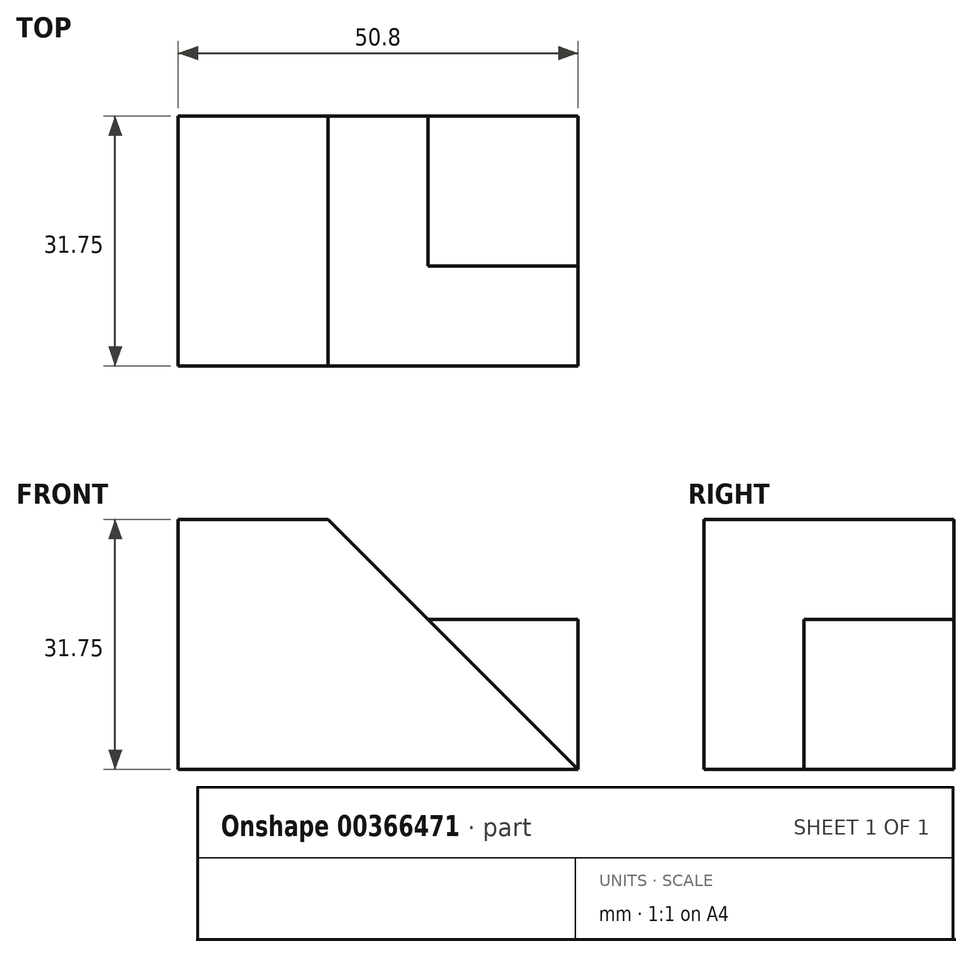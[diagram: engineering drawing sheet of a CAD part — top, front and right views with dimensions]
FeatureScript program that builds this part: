
annotation { "Feature Type Name" : "Feature", "Feature Type Description" : "" }
export const myFeature = defineFeature(function(context is Context, id is Id, definition is map)
    precondition{}
    {
        {
            var Q0;
            Q0=qCreatedBy(makeId("Front.planeOp"),FACE);
            var sketch = newSketch(context, id + "F0", { "sketchPlane" : qUnion([Q0])});
            skLineSegment(sketch, "E0", {"start": v(0, 0) * mm, "end": v(0, 31.75) * mm});
            skLineSegment(sketch, "E1", {"start": v(0, 31.75) * mm, "end": v(19.05, 31.75) * mm});
            skLineSegment(sketch, "E2", {"start": v(19.05, 31.75) * mm, "end": v(50.8, 0) * mm});
            skLineSegment(sketch, "E3", {"start": v(50.8, 0) * mm, "end": v(0, 0) * mm});
            skSolve(sketch);
        }
        {
            var Q0;
            Q0=makeQuery(id+"F0.imprint","IMPRINT",FACE,{"disambiguationData":[TD([[makeQuery(id+"F0.imprint","IMPRINT",EDGE,{"derivedFrom":sQuery(id+"F0.wireOp",EDGE,"E0")}),-1.0]])]});
            extrude(context, id + "F1", {"entities" : qUnion([Q0]), "oppositeDirection" : true, "depth" : 31.75 * mm});
        }
        {
            var Q0;
            Q0=makeQuery(id+"F1.opExtrude","CAP_FACE",FACE,{"disambiguationData":[OSD([sQuery(id+"F0.wireOp",EDGE,"E0"),sQuery(id+"F0.wireOp",EDGE,"E1"),sQuery(id+"F0.wireOp",EDGE,"E2"),sQuery(id+"F0.wireOp",EDGE,"E3")])],"isStart":false});
            var sketch = newSketch(context, id + "F2", { "sketchPlane" : qUnion([Q0])});
            skLineSegment(sketch, "E4", {"start": v(-50.8, 0) * mm, "end": v(-50.8, 19.05) * mm});
            skLineSegment(sketch, "E5", {"start": v(-50.8, 19.05) * mm, "end": v(-31.75, 19.05) * mm});
            skSolve(sketch);
        }
        {
            var Q0;
            Q0 = qSketchRegion(id + "F2", true);
            var Q1;
            {var subQ0=sQuery(id+"F2.wireOp",EDGE,"E4");Q1=makeQuery(id+"F2.imprint","IMPRINT",FACE,{"disambiguationData":[TD([[makeQuery(id+"F2.imprint","IMPRINT",EDGE,{"derivedFrom":subQ0}),-1.0]])]});}
            extrude(context, id + "F3", {"entities" : qUnion([Q0, Q1]), "operationType" : NewBodyOperationType.ADD, "oppositeDirection" : true, "depth" : 19.05 * mm});
        }
    });
